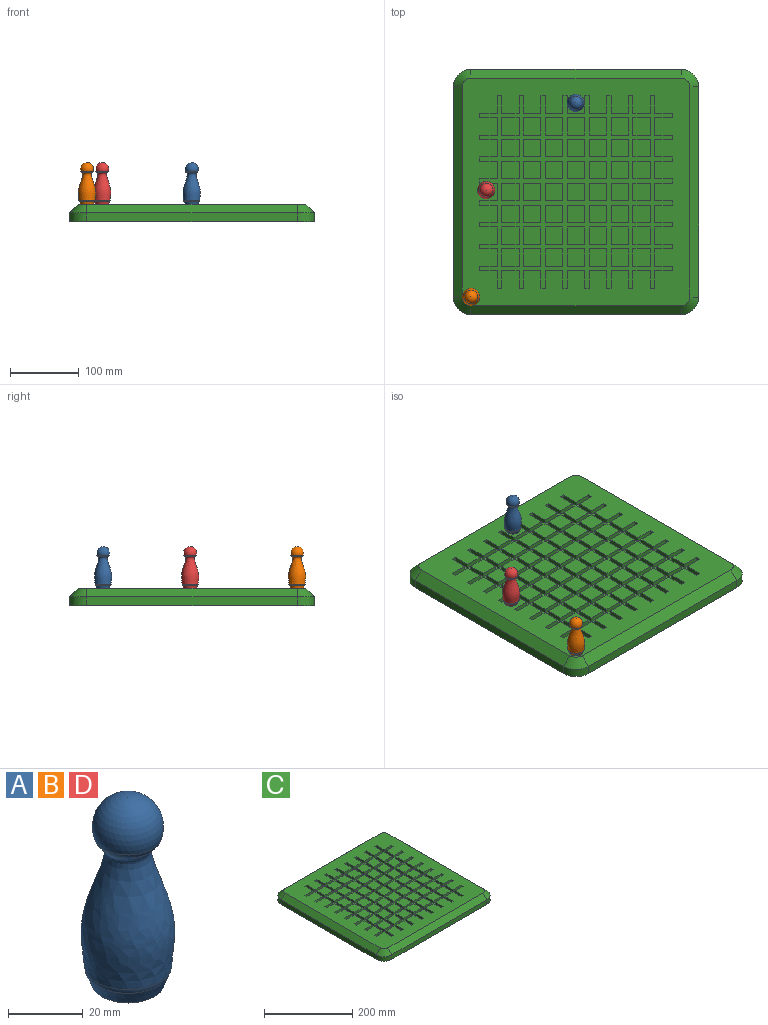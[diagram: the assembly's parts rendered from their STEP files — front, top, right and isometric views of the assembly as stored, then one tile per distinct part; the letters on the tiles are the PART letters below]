
ASSEMBLY  parts=4 mates=3
PART A: 6 faces, bbox 25.3x25.3x60.3 mm
  f0: revolved ~40.78x25.1mm, area 2684.5mm2, adj f4,f5
  f1: plane 19.67x19.67mm, normal (0,0,-1), area 303.8mm2, adj f3
  f2: sphere r=9.53mm, area 743.3mm2, adj f5
  f3: cone r=11.63mm half-angle=20deg, axis (0,0,1), area 301.1mm2, adj f1,f4
  f4: torus R=6.29mm, axis (0,0,-1), area 101.8mm2, adj f0,f3
  f5: torus R=3.91mm, axis (0,0,1), area 93.5mm2, adj f0,f2
PART B: same geometry as A
PART C: 388 faces, bbox 355.6x355.6x25.4 mm
  f0: plane 304.8x12.7mm, normal (0,-1,0), area 3871mm2, adj f4,f376,f379,f381
  f1: plane 304.8x12.7mm, normal (-1,0,0), area 3871mm2, adj f4,f376,f377,f382
  f2: plane 304.8x12.7mm, normal (0,1,0), area 3871mm2, adj f4,f377,f378,f386
  f3: plane 304.8x12.7mm, normal (1,0,0), area 3871mm2, adj f4,f378,f379,f385
  f4: plane 355.6x355.6mm, normal (0,0,-1), area 125897.5mm2, adj f0,f1,f2,f3,f376,f377,f378,f379
  f5: plane 25.4x6.35mm, normal (1,0,0), area 161.3mm2, adj f6,f8,f129,f130
  f6: plane 25.4x6.35mm, normal (0,1,0), area 161.3mm2, adj f5,f7,f129,f130
  f7: plane 6.35x6.35mm, normal (1,0,0), area 40.3mm2, adj f6,f98,f129,f130
  f8: plane 6.35x6.35mm, normal (0,1,0), area 40.3mm2, adj f5,f37,f129,f130
  f9: plane 25.4x6.35mm, normal (0,1,0), area 161.3mm2, adj f11,f12,f129,f130
  f10: plane 25.4x6.35mm, normal (0,-1,0), area 161.3mm2, adj f11,f95,f129,f130
  f11: plane 25.4x6.35mm, normal (1,0,0), area 161.3mm2, adj f9,f10,f129,f130
  f12: plane 6.35x6.35mm, normal (1,0,0), area 40.3mm2, adj f9,f14,f129,f130
  f13: plane 25.4x6.35mm, normal (0,1,0), area 161.3mm2, adj f15,f16,f129,f130
  f14: plane 25.4x6.35mm, normal (0,-1,0), area 161.3mm2, adj f12,f15,f129,f130
  f15: plane 25.4x6.35mm, normal (1,0,0), area 161.3mm2, adj f13,f14,f129,f130
  f16: plane 6.35x6.35mm, normal (1,0,0), area 40.3mm2, adj f13,f18,f129,f130
  f17: plane 25.4x6.35mm, normal (0,1,0), area 161.3mm2, adj f19,f20,f129,f130
  f18: plane 25.4x6.35mm, normal (0,-1,0), area 161.3mm2, adj f16,f19,f129,f130
  f19: plane 25.4x6.35mm, normal (1,0,0), area 161.3mm2, adj f17,f18,f129,f130
  f20: plane 6.35x6.35mm, normal (1,0,0), area 40.3mm2, adj f17,f22,f129,f130
  f21: plane 25.4x6.35mm, normal (0,1,0), area 161.3mm2, adj f23,f24,f129,f130
  f22: plane 25.4x6.35mm, normal (0,-1,0), area 161.3mm2, adj f20,f23,f129,f130
  f23: plane 25.4x6.35mm, normal (1,0,0), area 161.3mm2, adj f21,f22,f129,f130
  f24: plane 6.35x6.35mm, normal (1,0,0), area 40.3mm2, adj f21,f26,f129,f130
  f25: plane 25.4x6.35mm, normal (0,1,0), area 161.3mm2, adj f27,f28,f129,f130
  f26: plane 25.4x6.35mm, normal (0,-1,0), area 161.3mm2, adj f24,f27,f129,f130
  f27: plane 25.4x6.35mm, normal (1,0,0), area 161.3mm2, adj f25,f26,f129,f130
  f28: plane 6.35x6.35mm, normal (1,0,0), area 40.3mm2, adj f25,f30,f129,f130
  f29: plane 25.4x6.35mm, normal (0,1,0), area 161.3mm2, adj f31,f32,f129,f130
  f30: plane 25.4x6.35mm, normal (0,-1,0), area 161.3mm2, adj f28,f31,f129,f130
  f31: plane 25.4x6.35mm, normal (1,0,0), area 161.3mm2, adj f29,f30,f129,f130
  f32: plane 6.35x6.35mm, normal (1,0,0), area 40.3mm2, adj f29,f33,f129,f130
  f33: plane 25.4x6.35mm, normal (0,-1,0), area 161.3mm2, adj f32,f34,f129,f130
  f34: plane 25.4x6.35mm, normal (1,0,0), area 161.3mm2, adj f33,f35,f129,f130
  f35: plane 6.35x6.35mm, normal (0,-1,0), area 40.3mm2, adj f34,f40,f129,f130
  f36: plane 25.4x6.35mm, normal (0,1,0), area 161.3mm2, adj f37,f38,f129,f130
  f37: plane 25.4x6.35mm, normal (-1,0,0), area 161.3mm2, adj f8,f36,f129,f130
  f38: plane 25.4x6.35mm, normal (1,0,0), area 161.3mm2, adj f36,f39,f129,f130
  f39: plane 6.35x6.35mm, normal (0,1,0), area 40.3mm2, adj f38,f45,f129,f130
  f40: plane 25.4x6.35mm, normal (-1,0,0), area 161.3mm2, adj f35,f41,f129,f130
  f41: plane 25.4x6.35mm, normal (0,-1,0), area 161.3mm2, adj f40,f42,f129,f130
  f42: plane 25.4x6.35mm, normal (1,0,0), area 161.3mm2, adj f41,f43,f129,f130
  f43: plane 6.35x6.35mm, normal (0,-1,0), area 40.3mm2, adj f42,f48,f129,f130
  f44: plane 25.4x6.35mm, normal (0,1,0), area 161.3mm2, adj f45,f46,f129,f130
  f45: plane 25.4x6.35mm, normal (-1,0,0), area 161.3mm2, adj f39,f44,f129,f130
  f46: plane 25.4x6.35mm, normal (1,0,0), area 161.3mm2, adj f44,f47,f129,f130
  f47: plane 6.35x6.35mm, normal (0,1,0), area 40.3mm2, adj f46,f101,f129,f130
  f48: plane 25.4x6.35mm, normal (-1,0,0), area 161.3mm2, adj f43,f49,f129,f130
  f49: plane 25.4x6.35mm, normal (0,-1,0), area 161.3mm2, adj f48,f50,f129,f130
  f50: plane 25.4x6.35mm, normal (1,0,0), area 161.3mm2, adj f49,f51,f129,f130
  f51: plane 6.35x6.35mm, normal (0,-1,0), area 40.3mm2, adj f50,f52,f129,f130
  f52: plane 25.4x6.35mm, normal (-1,0,0), area 161.3mm2, adj f51,f53,f129,f130
  f53: plane 25.4x6.35mm, normal (0,-1,0), area 161.3mm2, adj f52,f54,f129,f130
  f54: plane 25.4x6.35mm, normal (1,0,0), area 161.3mm2, adj f53,f55,f129,f130
  f55: plane 6.35x6.35mm, normal (0,-1,0), area 40.3mm2, adj f54,f56,f129,f130
  f56: plane 25.4x6.35mm, normal (-1,0,0), area 161.3mm2, adj f55,f57,f129,f130
  f57: plane 25.4x6.35mm, normal (0,-1,0), area 161.3mm2, adj f56,f58,f129,f130
  f58: plane 25.4x6.35mm, normal (1,0,0), area 161.3mm2, adj f57,f59,f129,f130
  f59: plane 6.35x6.35mm, normal (0,-1,0), area 40.3mm2, adj f58,f60,f129,f130
  f60: plane 25.4x6.35mm, normal (-1,0,0), area 161.3mm2, adj f59,f61,f129,f130
  f61: plane 25.4x6.35mm, normal (0,-1,0), area 161.3mm2, adj f60,f62,f129,f130
  f62: plane 25.4x6.35mm, normal (1,0,0), area 161.3mm2, adj f61,f63,f129,f130
  f63: plane 6.35x6.35mm, normal (0,-1,0), area 40.3mm2, adj f62,f64,f129,f130
  f64: plane 25.4x6.35mm, normal (-1,0,0), area 161.3mm2, adj f63,f65,f129,f130
  f65: plane 25.4x6.35mm, normal (0,-1,0), area 161.3mm2, adj f64,f66,f129,f130
  f66: plane 25.4x6.35mm, normal (1,0,0), area 161.3mm2, adj f65,f67,f129,f130
  f67: plane 6.35x6.35mm, normal (0,-1,0), area 40.3mm2, adj f66,f68,f129,f130
  f68: plane 25.4x6.35mm, normal (-1,0,0), area 161.3mm2, adj f67,f69,f129,f130
  f69: plane 25.4x6.35mm, normal (0,-1,0), area 161.3mm2, adj f68,f70,f129,f130
  f70: plane 25.4x6.35mm, normal (1,0,0), area 161.3mm2, adj f69,f71,f129,f130
  f71: plane 6.35x6.35mm, normal (0,-1,0), area 40.3mm2, adj f70,f84,f129,f130
  f72: plane 25.4x6.35mm, normal (0,1,0), area 161.3mm2, adj f73,f75,f129,f130
  f73: plane 25.4x6.35mm, normal (-1,0,0), area 161.3mm2, adj f72,f74,f129,f130
  f74: plane 25.4x6.35mm, normal (0,-1,0), area 161.3mm2, adj f73,f96,f129,f130
  f75: plane 6.35x6.35mm, normal (-1,0,0), area 40.3mm2, adj f72,f78,f129,f130
  f76: plane 25.4x6.35mm, normal (0,1,0), area 161.3mm2, adj f77,f79,f129,f130
  f77: plane 25.4x6.35mm, normal (-1,0,0), area 161.3mm2, adj f76,f78,f129,f130
  f78: plane 25.4x6.35mm, normal (0,-1,0), area 161.3mm2, adj f75,f77,f129,f130
  f79: plane 6.35x6.35mm, normal (-1,0,0), area 40.3mm2, adj f76,f82,f129,f130
  f80: plane 25.4x6.35mm, normal (0,1,0), area 161.3mm2, adj f81,f83,f129,f130
  f81: plane 25.4x6.35mm, normal (-1,0,0), area 161.3mm2, adj f80,f82,f129,f130
  f82: plane 25.4x6.35mm, normal (0,-1,0), area 161.3mm2, adj f79,f81,f129,f130
  f83: plane 6.35x6.35mm, normal (-1,0,0), area 40.3mm2, adj f80,f85,f129,f130
  f84: plane 25.4x6.35mm, normal (-1,0,0), area 161.3mm2, adj f71,f85,f129,f130
  f85: plane 25.4x6.35mm, normal (0,-1,0), area 161.3mm2, adj f83,f84,f129,f130
  f86: plane 6.35x6.35mm, normal (0,1,0), area 40.3mm2, adj f105,f127,f129,f130
  f87: plane 6.35x6.35mm, normal (-1,0,0), area 40.3mm2, adj f120,f125,f129,f130
  f88: plane 6.35x6.35mm, normal (-1,0,0), area 40.3mm2, adj f117,f122,f129,f130
  f89: plane 6.35x6.35mm, normal (-1,0,0), area 40.3mm2, adj f114,f119,f129,f130
  f90: plane 6.35x6.35mm, normal (-1,0,0), area 40.3mm2, adj f112,f116,f129,f130
  f91: plane 6.35x6.35mm, normal (0,1,0), area 40.3mm2, adj f111,f113,f129,f130
  f92: plane 6.35x6.35mm, normal (0,1,0), area 40.3mm2, adj f108,f110,f129,f130
  f93: plane 6.35x6.35mm, normal (0,1,0), area 40.3mm2, adj f107,f128,f129,f130
  f94: plane 6.35x6.35mm, normal (0,1,0), area 40.3mm2, adj f102,f104,f129,f130
  f95: plane 6.35x6.35mm, normal (1,0,0), area 40.3mm2, adj f10,f97,f129,f130
  f96: plane 6.35x6.35mm, normal (-1,0,0), area 40.3mm2, adj f74,f123,f129,f130
  f97: plane 25.4x6.35mm, normal (0,1,0), area 161.3mm2, adj f95,f99,f129,f130
  f98: plane 25.4x6.35mm, normal (0,-1,0), area 161.3mm2, adj f7,f99,f129,f130
  f99: plane 25.4x6.35mm, normal (1,0,0), area 161.3mm2, adj f97,f98,f129,f130
  f100: plane 25.4x6.35mm, normal (0,1,0), area 161.3mm2, adj f101,f102,f129,f130
  f101: plane 25.4x6.35mm, normal (-1,0,0), area 161.3mm2, adj f47,f100,f129,f130
  f102: plane 25.4x6.35mm, normal (1,0,0), area 161.3mm2, adj f94,f100,f129,f130
  f103: plane 25.4x6.35mm, normal (0,1,0), area 161.3mm2, adj f104,f105,f129,f130
  f104: plane 25.4x6.35mm, normal (-1,0,0), area 161.3mm2, adj f94,f103,f129,f130
  f105: plane 25.4x6.35mm, normal (1,0,0), area 161.3mm2, adj f86,f103,f129,f130
  f106: plane 25.4x6.35mm, normal (0,1,0), area 161.3mm2, adj f107,f108,f129,f130
  f107: plane 25.4x6.35mm, normal (-1,0,0), area 161.3mm2, adj f93,f106,f129,f130
  f108: plane 25.4x6.35mm, normal (1,0,0), area 161.3mm2, adj f92,f106,f129,f130
  f109: plane 25.4x6.35mm, normal (0,1,0), area 161.3mm2, adj f110,f111,f129,f130
  f110: plane 25.4x6.35mm, normal (-1,0,0), area 161.3mm2, adj f92,f109,f129,f130
  f111: plane 25.4x6.35mm, normal (1,0,0), area 161.3mm2, adj f91,f109,f129,f130
  f112: plane 25.4x6.35mm, normal (0,1,0), area 161.3mm2, adj f90,f113,f129,f130
  f113: plane 25.4x6.35mm, normal (-1,0,0), area 161.3mm2, adj f91,f112,f129,f130
  f114: plane 25.4x6.35mm, normal (0,1,0), area 161.3mm2, adj f89,f115,f129,f130
  f115: plane 25.4x6.35mm, normal (-1,0,0), area 161.3mm2, adj f114,f116,f129,f130
  f116: plane 25.4x6.35mm, normal (0,-1,0), area 161.3mm2, adj f90,f115,f129,f130
  f117: plane 25.4x6.35mm, normal (0,1,0), area 161.3mm2, adj f88,f118,f129,f130
  f118: plane 25.4x6.35mm, normal (-1,0,0), area 161.3mm2, adj f117,f119,f129,f130
  f119: plane 25.4x6.35mm, normal (0,-1,0), area 161.3mm2, adj f89,f118,f129,f130
  f120: plane 25.4x6.35mm, normal (0,1,0), area 161.3mm2, adj f87,f121,f129,f130
  f121: plane 25.4x6.35mm, normal (-1,0,0), area 161.3mm2, adj f120,f122,f129,f130
  f122: plane 25.4x6.35mm, normal (0,-1,0), area 161.3mm2, adj f88,f121,f129,f130
  f123: plane 25.4x6.35mm, normal (0,1,0), area 161.3mm2, adj f96,f124,f129,f130
  f124: plane 25.4x6.35mm, normal (-1,0,0), area 161.3mm2, adj f123,f125,f129,f130
  f125: plane 25.4x6.35mm, normal (0,-1,0), area 161.3mm2, adj f87,f124,f129,f130
  f126: plane 25.4x6.35mm, normal (0,1,0), area 161.3mm2, adj f127,f128,f129,f130
  f127: plane 25.4x6.35mm, normal (-1,0,0), area 161.3mm2, adj f86,f126,f129,f130
  f128: plane 25.4x6.35mm, normal (1,0,0), area 161.3mm2, adj f93,f126,f129,f130
  f129: plane 330.2x330.2mm, normal (0,0,1), area 51474.3mm2, adj f5,f6,f7,f8,f9,f10,f11,f12
  f130: plane 279.4x279.4mm, normal (0,0,1), area 25806.4mm2, adj f5,f6,f7,f8,f9,f10,f11,f12
  f131: plane 25.4x6.35mm, normal (0,1,0), area 161.3mm2, adj f130,f132,f134,f135
  f132: plane 25.4x6.35mm, normal (-1,0,0), area 161.3mm2, adj f130,f131,f133,f135
  f133: plane 25.4x6.35mm, normal (0,-1,0), area 161.3mm2, adj f130,f132,f134,f135
  f134: plane 25.4x6.35mm, normal (1,0,0), area 161.3mm2, adj f130,f131,f133,f135
  f135: plane 25.4x25.4mm, normal (0,0,1), area 645.2mm2, adj f131,f132,f133,f134
  f136: plane 25.4x6.35mm, normal (0,1,0), area 161.3mm2, adj f130,f137,f139,f140
  f137: plane 25.4x6.35mm, normal (-1,0,0), area 161.3mm2, adj f130,f136,f138,f140
  f138: plane 25.4x6.35mm, normal (0,-1,0), area 161.3mm2, adj f130,f137,f139,f140
  f139: plane 25.4x6.35mm, normal (1,0,0), area 161.3mm2, adj f130,f136,f138,f140
  f140: plane 25.4x25.4mm, normal (0,0,1), area 645.2mm2, adj f136,f137,f138,f139
  f141: plane 25.4x6.35mm, normal (0,1,0), area 161.3mm2, adj f130,f142,f144,f145
  f142: plane 25.4x6.35mm, normal (-1,0,0), area 161.3mm2, adj f130,f141,f143,f145
  f143: plane 25.4x6.35mm, normal (0,-1,0), area 161.3mm2, adj f130,f142,f144,f145
  f144: plane 25.4x6.35mm, normal (1,0,0), area 161.3mm2, adj f130,f141,f143,f145
  f145: plane 25.4x25.4mm, normal (0,0,1), area 645.2mm2, adj f141,f142,f143,f144
  f146: plane 25.4x6.35mm, normal (0,1,0), area 161.3mm2, adj f130,f147,f149,f150
  f147: plane 25.4x6.35mm, normal (-1,0,0), area 161.3mm2, adj f130,f146,f148,f150
  f148: plane 25.4x6.35mm, normal (0,-1,0), area 161.3mm2, adj f130,f147,f149,f150
  f149: plane 25.4x6.35mm, normal (1,0,0), area 161.3mm2, adj f130,f146,f148,f150
  f150: plane 25.4x25.4mm, normal (0,0,1), area 645.2mm2, adj f146,f147,f148,f149
  f151: plane 25.4x6.35mm, normal (0,1,0), area 161.3mm2, adj f130,f152,f154,f155
  f152: plane 25.4x6.35mm, normal (-1,0,0), area 161.3mm2, adj f130,f151,f153,f155
  f153: plane 25.4x6.35mm, normal (0,-1,0), area 161.3mm2, adj f130,f152,f154,f155
  f154: plane 25.4x6.35mm, normal (1,0,0), area 161.3mm2, adj f130,f151,f153,f155
  f155: plane 25.4x25.4mm, normal (0,0,1), area 645.2mm2, adj f151,f152,f153,f154
  f156: plane 25.4x6.35mm, normal (0,1,0), area 161.3mm2, adj f130,f157,f159,f160
  f157: plane 25.4x6.35mm, normal (-1,0,0), area 161.3mm2, adj f130,f156,f158,f160
  f158: plane 25.4x6.35mm, normal (0,-1,0), area 161.3mm2, adj f130,f157,f159,f160
  f159: plane 25.4x6.35mm, normal (1,0,0), area 161.3mm2, adj f130,f156,f158,f160
  f160: plane 25.4x25.4mm, normal (0,0,1), area 645.2mm2, adj f156,f157,f158,f159
  f161: plane 25.4x6.35mm, normal (0,1,0), area 161.3mm2, adj f130,f162,f164,f165
  f162: plane 25.4x6.35mm, normal (-1,0,0), area 161.3mm2, adj f130,f161,f163,f165
  f163: plane 25.4x6.35mm, normal (0,-1,0), area 161.3mm2, adj f130,f162,f164,f165
  f164: plane 25.4x6.35mm, normal (1,0,0), area 161.3mm2, adj f130,f161,f163,f165
  f165: plane 25.4x25.4mm, normal (0,0,1), area 645.2mm2, adj f161,f162,f163,f164
  f166: plane 25.4x6.35mm, normal (0,1,0), area 161.3mm2, adj f130,f167,f169,f170
  f167: plane 25.4x6.35mm, normal (-1,0,0), area 161.3mm2, adj f130,f166,f168,f170
  f168: plane 25.4x6.35mm, normal (0,-1,0), area 161.3mm2, adj f130,f167,f169,f170
  f169: plane 25.4x6.35mm, normal (1,0,0), area 161.3mm2, adj f130,f166,f168,f170
  f170: plane 25.4x25.4mm, normal (0,0,1), area 645.2mm2, adj f166,f167,f168,f169
  f171: plane 25.4x6.35mm, normal (0,1,0), area 161.3mm2, adj f130,f172,f174,f175
  f172: plane 25.4x6.35mm, normal (-1,0,0), area 161.3mm2, adj f130,f171,f173,f175
  f173: plane 25.4x6.35mm, normal (0,-1,0), area 161.3mm2, adj f130,f172,f174,f175
  f174: plane 25.4x6.35mm, normal (1,0,0), area 161.3mm2, adj f130,f171,f173,f175
  f175: plane 25.4x25.4mm, normal (0,0,1), area 645.2mm2, adj f171,f172,f173,f174
  f176: plane 25.4x6.35mm, normal (0,1,0), area 161.3mm2, adj f130,f177,f179,f180
  f177: plane 25.4x6.35mm, normal (-1,0,0), area 161.3mm2, adj f130,f176,f178,f180
  f178: plane 25.4x6.35mm, normal (0,-1,0), area 161.3mm2, adj f130,f177,f179,f180
  f179: plane 25.4x6.35mm, normal (1,0,0), area 161.3mm2, adj f130,f176,f178,f180
  f180: plane 25.4x25.4mm, normal (0,0,1), area 645.2mm2, adj f176,f177,f178,f179
  f181: plane 25.4x6.35mm, normal (0,1,0), area 161.3mm2, adj f130,f182,f184,f185
  f182: plane 25.4x6.35mm, normal (-1,0,0), area 161.3mm2, adj f130,f181,f183,f185
  f183: plane 25.4x6.35mm, normal (0,-1,0), area 161.3mm2, adj f130,f182,f184,f185
  f184: plane 25.4x6.35mm, normal (1,0,0), area 161.3mm2, adj f130,f181,f183,f185
  f185: plane 25.4x25.4mm, normal (0,0,1), area 645.2mm2, adj f181,f182,f183,f184
  f186: plane 25.4x6.35mm, normal (0,1,0), area 161.3mm2, adj f130,f187,f189,f190
  f187: plane 25.4x6.35mm, normal (-1,0,0), area 161.3mm2, adj f130,f186,f188,f190
  f188: plane 25.4x6.35mm, normal (0,-1,0), area 161.3mm2, adj f130,f187,f189,f190
  f189: plane 25.4x6.35mm, normal (1,0,0), area 161.3mm2, adj f130,f186,f188,f190
  f190: plane 25.4x25.4mm, normal (0,0,1), area 645.2mm2, adj f186,f187,f188,f189
  f191: plane 25.4x6.35mm, normal (0,1,0), area 161.3mm2, adj f130,f192,f194,f195
  f192: plane 25.4x6.35mm, normal (-1,0,0), area 161.3mm2, adj f130,f191,f193,f195
  f193: plane 25.4x6.35mm, normal (0,-1,0), area 161.3mm2, adj f130,f192,f194,f195
  f194: plane 25.4x6.35mm, normal (1,0,0), area 161.3mm2, adj f130,f191,f193,f195
  f195: plane 25.4x25.4mm, normal (0,0,1), area 645.2mm2, adj f191,f192,f193,f194
  f196: plane 25.4x6.35mm, normal (0,1,0), area 161.3mm2, adj f130,f197,f199,f200
  f197: plane 25.4x6.35mm, normal (-1,0,0), area 161.3mm2, adj f130,f196,f198,f200
  f198: plane 25.4x6.35mm, normal (0,-1,0), area 161.3mm2, adj f130,f197,f199,f200
  f199: plane 25.4x6.35mm, normal (1,0,0), area 161.3mm2, adj f130,f196,f198,f200
  f200: plane 25.4x25.4mm, normal (0,0,1), area 645.2mm2, adj f196,f197,f198,f199
  f201: plane 25.4x6.35mm, normal (0,1,0), area 161.3mm2, adj f130,f202,f204,f205
  f202: plane 25.4x6.35mm, normal (-1,0,0), area 161.3mm2, adj f130,f201,f203,f205
  f203: plane 25.4x6.35mm, normal (0,-1,0), area 161.3mm2, adj f130,f202,f204,f205
  f204: plane 25.4x6.35mm, normal (1,0,0), area 161.3mm2, adj f130,f201,f203,f205
  f205: plane 25.4x25.4mm, normal (0,0,1), area 645.2mm2, adj f201,f202,f203,f204
  f206: plane 25.4x6.35mm, normal (0,1,0), area 161.3mm2, adj f130,f207,f209,f210
  f207: plane 25.4x6.35mm, normal (-1,0,0), area 161.3mm2, adj f130,f206,f208,f210
  f208: plane 25.4x6.35mm, normal (0,-1,0), area 161.3mm2, adj f130,f207,f209,f210
  f209: plane 25.4x6.35mm, normal (1,0,0), area 161.3mm2, adj f130,f206,f208,f210
  f210: plane 25.4x25.4mm, normal (0,0,1), area 645.2mm2, adj f206,f207,f208,f209
  f211: plane 25.4x6.35mm, normal (0,1,0), area 161.3mm2, adj f130,f212,f214,f215
  f212: plane 25.4x6.35mm, normal (-1,0,0), area 161.3mm2, adj f130,f211,f213,f215
  f213: plane 25.4x6.35mm, normal (0,-1,0), area 161.3mm2, adj f130,f212,f214,f215
  f214: plane 25.4x6.35mm, normal (1,0,0), area 161.3mm2, adj f130,f211,f213,f215
  f215: plane 25.4x25.4mm, normal (0,0,1), area 645.2mm2, adj f211,f212,f213,f214
  f216: plane 25.4x6.35mm, normal (0,1,0), area 161.3mm2, adj f130,f217,f219,f220
  f217: plane 25.4x6.35mm, normal (-1,0,0), area 161.3mm2, adj f130,f216,f218,f220
  f218: plane 25.4x6.35mm, normal (0,-1,0), area 161.3mm2, adj f130,f217,f219,f220
  f219: plane 25.4x6.35mm, normal (1,0,0), area 161.3mm2, adj f130,f216,f218,f220
  f220: plane 25.4x25.4mm, normal (0,0,1), area 645.2mm2, adj f216,f217,f218,f219
  f221: plane 25.4x6.35mm, normal (0,1,0), area 161.3mm2, adj f130,f222,f224,f225
  f222: plane 25.4x6.35mm, normal (-1,0,0), area 161.3mm2, adj f130,f221,f223,f225
  f223: plane 25.4x6.35mm, normal (0,-1,0), area 161.3mm2, adj f130,f222,f224,f225
  f224: plane 25.4x6.35mm, normal (1,0,0), area 161.3mm2, adj f130,f221,f223,f225
  f225: plane 25.4x25.4mm, normal (0,0,1), area 645.2mm2, adj f221,f222,f223,f224
  f226: plane 25.4x6.35mm, normal (0,1,0), area 161.3mm2, adj f130,f227,f229,f230
  f227: plane 25.4x6.35mm, normal (-1,0,0), area 161.3mm2, adj f130,f226,f228,f230
  f228: plane 25.4x6.35mm, normal (0,-1,0), area 161.3mm2, adj f130,f227,f229,f230
  f229: plane 25.4x6.35mm, normal (1,0,0), area 161.3mm2, adj f130,f226,f228,f230
  f230: plane 25.4x25.4mm, normal (0,0,1), area 645.2mm2, adj f226,f227,f228,f229
  f231: plane 25.4x6.35mm, normal (0,1,0), area 161.3mm2, adj f130,f232,f234,f235
  f232: plane 25.4x6.35mm, normal (-1,0,0), area 161.3mm2, adj f130,f231,f233,f235
  f233: plane 25.4x6.35mm, normal (0,-1,0), area 161.3mm2, adj f130,f232,f234,f235
  f234: plane 25.4x6.35mm, normal (1,0,0), area 161.3mm2, adj f130,f231,f233,f235
  f235: plane 25.4x25.4mm, normal (0,0,1), area 645.2mm2, adj f231,f232,f233,f234
  f236: plane 25.4x6.35mm, normal (0,1,0), area 161.3mm2, adj f130,f237,f239,f240
  f237: plane 25.4x6.35mm, normal (-1,0,0), area 161.3mm2, adj f130,f236,f238,f240
  f238: plane 25.4x6.35mm, normal (0,-1,0), area 161.3mm2, adj f130,f237,f239,f240
  f239: plane 25.4x6.35mm, normal (1,0,0), area 161.3mm2, adj f130,f236,f238,f240
  f240: plane 25.4x25.4mm, normal (0,0,1), area 645.2mm2, adj f236,f237,f238,f239
  f241: plane 25.4x6.35mm, normal (0,1,0), area 161.3mm2, adj f130,f242,f244,f245
  f242: plane 25.4x6.35mm, normal (-1,0,0), area 161.3mm2, adj f130,f241,f243,f245
  f243: plane 25.4x6.35mm, normal (0,-1,0), area 161.3mm2, adj f130,f242,f244,f245
  f244: plane 25.4x6.35mm, normal (1,0,0), area 161.3mm2, adj f130,f241,f243,f245
  f245: plane 25.4x25.4mm, normal (0,0,1), area 645.2mm2, adj f241,f242,f243,f244
  f246: plane 25.4x6.35mm, normal (0,1,0), area 161.3mm2, adj f130,f247,f249,f250
  f247: plane 25.4x6.35mm, normal (-1,0,0), area 161.3mm2, adj f130,f246,f248,f250
  f248: plane 25.4x6.35mm, normal (0,-1,0), area 161.3mm2, adj f130,f247,f249,f250
  f249: plane 25.4x6.35mm, normal (1,0,0), area 161.3mm2, adj f130,f246,f248,f250
  f250: plane 25.4x25.4mm, normal (0,0,1), area 645.2mm2, adj f246,f247,f248,f249
  f251: plane 25.4x6.35mm, normal (0,1,0), area 161.3mm2, adj f130,f252,f254,f255
  f252: plane 25.4x6.35mm, normal (-1,0,0), area 161.3mm2, adj f130,f251,f253,f255
  f253: plane 25.4x6.35mm, normal (0,-1,0), area 161.3mm2, adj f130,f252,f254,f255
  f254: plane 25.4x6.35mm, normal (1,0,0), area 161.3mm2, adj f130,f251,f253,f255
  f255: plane 25.4x25.4mm, normal (0,0,1), area 645.2mm2, adj f251,f252,f253,f254
  f256: plane 25.4x6.35mm, normal (0,1,0), area 161.3mm2, adj f130,f257,f259,f260
  f257: plane 25.4x6.35mm, normal (-1,0,0), area 161.3mm2, adj f130,f256,f258,f260
  f258: plane 25.4x6.35mm, normal (0,-1,0), area 161.3mm2, adj f130,f257,f259,f260
  f259: plane 25.4x6.35mm, normal (1,0,0), area 161.3mm2, adj f130,f256,f258,f260
  f260: plane 25.4x25.4mm, normal (0,0,1), area 645.2mm2, adj f256,f257,f258,f259
  f261: plane 25.4x6.35mm, normal (0,1,0), area 161.3mm2, adj f130,f262,f264,f265
  f262: plane 25.4x6.35mm, normal (-1,0,0), area 161.3mm2, adj f130,f261,f263,f265
  f263: plane 25.4x6.35mm, normal (0,-1,0), area 161.3mm2, adj f130,f262,f264,f265
  f264: plane 25.4x6.35mm, normal (1,0,0), area 161.3mm2, adj f130,f261,f263,f265
  f265: plane 25.4x25.4mm, normal (0,0,1), area 645.2mm2, adj f261,f262,f263,f264
  f266: plane 25.4x6.35mm, normal (0,1,0), area 161.3mm2, adj f130,f267,f269,f270
  f267: plane 25.4x6.35mm, normal (-1,0,0), area 161.3mm2, adj f130,f266,f268,f270
  f268: plane 25.4x6.35mm, normal (0,-1,0), area 161.3mm2, adj f130,f267,f269,f270
  f269: plane 25.4x6.35mm, normal (1,0,0), area 161.3mm2, adj f130,f266,f268,f270
  f270: plane 25.4x25.4mm, normal (0,0,1), area 645.2mm2, adj f266,f267,f268,f269
  f271: plane 25.4x6.35mm, normal (0,1,0), area 161.3mm2, adj f130,f272,f274,f275
  f272: plane 25.4x6.35mm, normal (-1,0,0), area 161.3mm2, adj f130,f271,f273,f275
  f273: plane 25.4x6.35mm, normal (0,-1,0), area 161.3mm2, adj f130,f272,f274,f275
  f274: plane 25.4x6.35mm, normal (1,0,0), area 161.3mm2, adj f130,f271,f273,f275
  f275: plane 25.4x25.4mm, normal (0,0,1), area 645.2mm2, adj f271,f272,f273,f274
  f276: plane 25.4x6.35mm, normal (0,1,0), area 161.3mm2, adj f130,f277,f279,f280
  f277: plane 25.4x6.35mm, normal (-1,0,0), area 161.3mm2, adj f130,f276,f278,f280
  f278: plane 25.4x6.35mm, normal (0,-1,0), area 161.3mm2, adj f130,f277,f279,f280
  f279: plane 25.4x6.35mm, normal (1,0,0), area 161.3mm2, adj f130,f276,f278,f280
  f280: plane 25.4x25.4mm, normal (0,0,1), area 645.2mm2, adj f276,f277,f278,f279
  f281: plane 25.4x6.35mm, normal (0,1,0), area 161.3mm2, adj f130,f282,f284,f285
  f282: plane 25.4x6.35mm, normal (-1,0,0), area 161.3mm2, adj f130,f281,f283,f285
  f283: plane 25.4x6.35mm, normal (0,-1,0), area 161.3mm2, adj f130,f282,f284,f285
  f284: plane 25.4x6.35mm, normal (1,0,0), area 161.3mm2, adj f130,f281,f283,f285
  f285: plane 25.4x25.4mm, normal (0,0,1), area 645.2mm2, adj f281,f282,f283,f284
  f286: plane 25.4x6.35mm, normal (0,1,0), area 161.3mm2, adj f130,f287,f289,f290
  f287: plane 25.4x6.35mm, normal (-1,0,0), area 161.3mm2, adj f130,f286,f288,f290
  f288: plane 25.4x6.35mm, normal (0,-1,0), area 161.3mm2, adj f130,f287,f289,f290
  f289: plane 25.4x6.35mm, normal (1,0,0), area 161.3mm2, adj f130,f286,f288,f290
  f290: plane 25.4x25.4mm, normal (0,0,1), area 645.2mm2, adj f286,f287,f288,f289
  f291: plane 25.4x6.35mm, normal (0,1,0), area 161.3mm2, adj f130,f292,f294,f295
  f292: plane 25.4x6.35mm, normal (-1,0,0), area 161.3mm2, adj f130,f291,f293,f295
  f293: plane 25.4x6.35mm, normal (0,-1,0), area 161.3mm2, adj f130,f292,f294,f295
  f294: plane 25.4x6.35mm, normal (1,0,0), area 161.3mm2, adj f130,f291,f293,f295
  f295: plane 25.4x25.4mm, normal (0,0,1), area 645.2mm2, adj f291,f292,f293,f294
  f296: plane 25.4x6.35mm, normal (0,1,0), area 161.3mm2, adj f130,f297,f299,f300
  f297: plane 25.4x6.35mm, normal (-1,0,0), area 161.3mm2, adj f130,f296,f298,f300
  f298: plane 25.4x6.35mm, normal (0,-1,0), area 161.3mm2, adj f130,f297,f299,f300
  f299: plane 25.4x6.35mm, normal (1,0,0), area 161.3mm2, adj f130,f296,f298,f300
  f300: plane 25.4x25.4mm, normal (0,0,1), area 645.2mm2, adj f296,f297,f298,f299
  f301: plane 25.4x6.35mm, normal (0,1,0), area 161.3mm2, adj f130,f302,f304,f305
  f302: plane 25.4x6.35mm, normal (-1,0,0), area 161.3mm2, adj f130,f301,f303,f305
  f303: plane 25.4x6.35mm, normal (0,-1,0), area 161.3mm2, adj f130,f302,f304,f305
  f304: plane 25.4x6.35mm, normal (1,0,0), area 161.3mm2, adj f130,f301,f303,f305
  f305: plane 25.4x25.4mm, normal (0,0,1), area 645.2mm2, adj f301,f302,f303,f304
  f306: plane 25.4x6.35mm, normal (0,1,0), area 161.3mm2, adj f130,f307,f309,f310
  f307: plane 25.4x6.35mm, normal (-1,0,0), area 161.3mm2, adj f130,f306,f308,f310
  f308: plane 25.4x6.35mm, normal (0,-1,0), area 161.3mm2, adj f130,f307,f309,f310
  f309: plane 25.4x6.35mm, normal (1,0,0), area 161.3mm2, adj f130,f306,f308,f310
  f310: plane 25.4x25.4mm, normal (0,0,1), area 645.2mm2, adj f306,f307,f308,f309
  f311: plane 25.4x6.35mm, normal (0,1,0), area 161.3mm2, adj f130,f312,f314,f315
  f312: plane 25.4x6.35mm, normal (-1,0,0), area 161.3mm2, adj f130,f311,f313,f315
  f313: plane 25.4x6.35mm, normal (0,-1,0), area 161.3mm2, adj f130,f312,f314,f315
  f314: plane 25.4x6.35mm, normal (1,0,0), area 161.3mm2, adj f130,f311,f313,f315
  f315: plane 25.4x25.4mm, normal (0,0,1), area 645.2mm2, adj f311,f312,f313,f314
  f316: plane 25.4x6.35mm, normal (0,1,0), area 161.3mm2, adj f130,f317,f319,f320
  f317: plane 25.4x6.35mm, normal (-1,0,0), area 161.3mm2, adj f130,f316,f318,f320
  f318: plane 25.4x6.35mm, normal (0,-1,0), area 161.3mm2, adj f130,f317,f319,f320
  f319: plane 25.4x6.35mm, normal (1,0,0), area 161.3mm2, adj f130,f316,f318,f320
  f320: plane 25.4x25.4mm, normal (0,0,1), area 645.2mm2, adj f316,f317,f318,f319
  f321: plane 25.4x6.35mm, normal (0,1,0), area 161.3mm2, adj f130,f322,f324,f325
  f322: plane 25.4x6.35mm, normal (-1,0,0), area 161.3mm2, adj f130,f321,f323,f325
  f323: plane 25.4x6.35mm, normal (0,-1,0), area 161.3mm2, adj f130,f322,f324,f325
  f324: plane 25.4x6.35mm, normal (1,0,0), area 161.3mm2, adj f130,f321,f323,f325
  f325: plane 25.4x25.4mm, normal (0,0,1), area 645.2mm2, adj f321,f322,f323,f324
  f326: plane 25.4x6.35mm, normal (0,1,0), area 161.3mm2, adj f130,f327,f329,f330
  f327: plane 25.4x6.35mm, normal (-1,0,0), area 161.3mm2, adj f130,f326,f328,f330
  f328: plane 25.4x6.35mm, normal (0,-1,0), area 161.3mm2, adj f130,f327,f329,f330
  f329: plane 25.4x6.35mm, normal (1,0,0), area 161.3mm2, adj f130,f326,f328,f330
  f330: plane 25.4x25.4mm, normal (0,0,1), area 645.2mm2, adj f326,f327,f328,f329
  f331: plane 25.4x6.35mm, normal (0,1,0), area 161.3mm2, adj f130,f332,f334,f335
  f332: plane 25.4x6.35mm, normal (-1,0,0), area 161.3mm2, adj f130,f331,f333,f335
  f333: plane 25.4x6.35mm, normal (0,-1,0), area 161.3mm2, adj f130,f332,f334,f335
  f334: plane 25.4x6.35mm, normal (1,0,0), area 161.3mm2, adj f130,f331,f333,f335
  f335: plane 25.4x25.4mm, normal (0,0,1), area 645.2mm2, adj f331,f332,f333,f334
  f336: plane 25.4x6.35mm, normal (0,1,0), area 161.3mm2, adj f130,f337,f339,f340
  f337: plane 25.4x6.35mm, normal (-1,0,0), area 161.3mm2, adj f130,f336,f338,f340
  f338: plane 25.4x6.35mm, normal (0,-1,0), area 161.3mm2, adj f130,f337,f339,f340
  f339: plane 25.4x6.35mm, normal (1,0,0), area 161.3mm2, adj f130,f336,f338,f340
  f340: plane 25.4x25.4mm, normal (0,0,1), area 645.2mm2, adj f336,f337,f338,f339
  f341: plane 25.4x6.35mm, normal (0,1,0), area 161.3mm2, adj f130,f342,f344,f345
  f342: plane 25.4x6.35mm, normal (-1,0,0), area 161.3mm2, adj f130,f341,f343,f345
  f343: plane 25.4x6.35mm, normal (0,-1,0), area 161.3mm2, adj f130,f342,f344,f345
  f344: plane 25.4x6.35mm, normal (1,0,0), area 161.3mm2, adj f130,f341,f343,f345
  f345: plane 25.4x25.4mm, normal (0,0,1), area 645.2mm2, adj f341,f342,f343,f344
  f346: plane 25.4x6.35mm, normal (0,1,0), area 161.3mm2, adj f130,f347,f349,f350
  f347: plane 25.4x6.35mm, normal (-1,0,0), area 161.3mm2, adj f130,f346,f348,f350
  f348: plane 25.4x6.35mm, normal (0,-1,0), area 161.3mm2, adj f130,f347,f349,f350
  f349: plane 25.4x6.35mm, normal (1,0,0), area 161.3mm2, adj f130,f346,f348,f350
  f350: plane 25.4x25.4mm, normal (0,0,1), area 645.2mm2, adj f346,f347,f348,f349
  f351: plane 25.4x6.35mm, normal (0,1,0), area 161.3mm2, adj f130,f352,f354,f355
  f352: plane 25.4x6.35mm, normal (-1,0,0), area 161.3mm2, adj f130,f351,f353,f355
  f353: plane 25.4x6.35mm, normal (0,-1,0), area 161.3mm2, adj f130,f352,f354,f355
  f354: plane 25.4x6.35mm, normal (1,0,0), area 161.3mm2, adj f130,f351,f353,f355
  f355: plane 25.4x25.4mm, normal (0,0,1), area 645.2mm2, adj f351,f352,f353,f354
  f356: plane 25.4x6.35mm, normal (0,1,0), area 161.3mm2, adj f130,f357,f359,f360
  f357: plane 25.4x6.35mm, normal (-1,0,0), area 161.3mm2, adj f130,f356,f358,f360
  f358: plane 25.4x6.35mm, normal (0,-1,0), area 161.3mm2, adj f130,f357,f359,f360
  f359: plane 25.4x6.35mm, normal (1,0,0), area 161.3mm2, adj f130,f356,f358,f360
  f360: plane 25.4x25.4mm, normal (0,0,1), area 645.2mm2, adj f356,f357,f358,f359
  f361: plane 25.4x6.35mm, normal (0,1,0), area 161.3mm2, adj f130,f362,f364,f365
  f362: plane 25.4x6.35mm, normal (-1,0,0), area 161.3mm2, adj f130,f361,f363,f365
  f363: plane 25.4x6.35mm, normal (0,-1,0), area 161.3mm2, adj f130,f362,f364,f365
  f364: plane 25.4x6.35mm, normal (1,0,0), area 161.3mm2, adj f130,f361,f363,f365
  f365: plane 25.4x25.4mm, normal (0,0,1), area 645.2mm2, adj f361,f362,f363,f364
  f366: plane 25.4x6.35mm, normal (0,1,0), area 161.3mm2, adj f130,f367,f369,f370
  f367: plane 25.4x6.35mm, normal (-1,0,0), area 161.3mm2, adj f130,f366,f368,f370
  f368: plane 25.4x6.35mm, normal (0,-1,0), area 161.3mm2, adj f130,f367,f369,f370
  f369: plane 25.4x6.35mm, normal (1,0,0), area 161.3mm2, adj f130,f366,f368,f370
  f370: plane 25.4x25.4mm, normal (0,0,1), area 645.2mm2, adj f366,f367,f368,f369
  f371: plane 25.4x6.35mm, normal (0,1,0), area 161.3mm2, adj f130,f372,f374,f375
  f372: plane 25.4x6.35mm, normal (-1,0,0), area 161.3mm2, adj f130,f371,f373,f375
  f373: plane 25.4x6.35mm, normal (0,-1,0), area 161.3mm2, adj f130,f372,f374,f375
  f374: plane 25.4x6.35mm, normal (1,0,0), area 161.3mm2, adj f130,f371,f373,f375
  f375: plane 25.4x25.4mm, normal (0,0,1), area 645.2mm2, adj f371,f372,f373,f374
  f376: cylinder r=25.4mm len=25.4mm, axis (0,0,1), area 506.7mm2, adj f0,f1,f4,f380
  f377: cylinder r=25.4mm len=25.4mm, axis (0,0,-1), area 506.7mm2, adj f1,f2,f4,f384
  f378: cylinder r=25.4mm len=25.4mm, axis (0,0,1), area 506.7mm2, adj f2,f3,f4,f387
  f379: cylinder r=25.4mm len=25.4mm, axis (0,0,-1), area 506.7mm2, adj f0,f3,f4,f383
  f380: cone r=12.7mm half-angle=45deg, axis (0,0,-1), area 537.4mm2, adj f129,f376,f381,f382
  f381: plane 304.8x12.7mm, normal (0,-0.71,0.71), area 5474.4mm2, adj f0,f129,f380,f383
  f382: plane 304.8x12.7mm, normal (-0.71,0,0.71), area 5474.4mm2, adj f1,f129,f380,f384
  f383: cone r=12.7mm half-angle=45deg, axis (0,0,-1), area 537.4mm2, adj f129,f379,f381,f385
  f384: cone r=12.7mm half-angle=45deg, axis (0,0,-1), area 537.4mm2, adj f129,f377,f382,f386
  f385: plane 304.8x12.7mm, normal (0.71,0,0.71), area 5474.4mm2, adj f3,f129,f383,f387
  f386: plane 304.8x12.7mm, normal (0,0.71,0.71), area 5474.4mm2, adj f2,f129,f384,f387
  f387: cone r=12.7mm half-angle=45deg, axis (0,0,-1), area 537.4mm2, adj f129,f378,f385,f386
PART D: same geometry as A
PLACE A t=(214.09,276.61,30.11)mm
PLACE B t=(62.2,-4.84,30.11)mm
PLACE C t=(74.9,7.86,4.71)mm
PLACE D t=(84.2,150.31,30.11)mm
MATE planar D.f3 <-> C.f129  axis (0,0,-1) through (84.2,150.31,30.11)mm
MATE planar B.f3 <-> C.f376  axis (0,0,-1) through (62.2,-4.84,30.11)mm
MATE planar A.f3 <-> C.f285  axis (0,0,-1) through (214.09,276.61,30.11)mm
